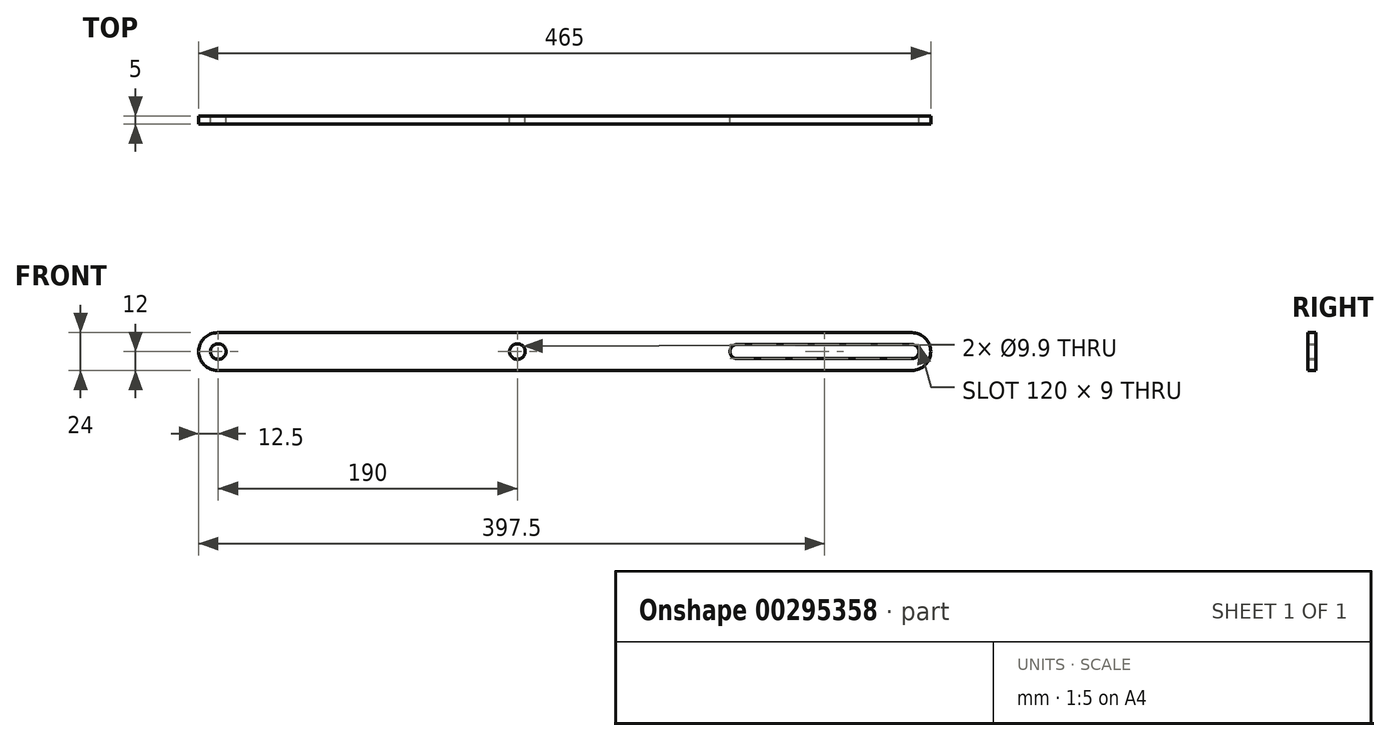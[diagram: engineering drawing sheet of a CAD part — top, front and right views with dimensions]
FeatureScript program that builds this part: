
annotation { "Feature Type Name" : "Feature", "Feature Type Description" : "" }
export const myFeature = defineFeature(function(context is Context, id is Id, definition is map)
    precondition{}
    {
        {
            var Q0;
            Q0=qCreatedBy(makeId("Front.planeOp"),FACE);
            var sketch = newSketch(context, id + "F0", { "sketchPlane" : qUnion([Q0])});
            skLineSegment(sketch, "E0.bottom", {"start": v(220.5, -12) * mm, "end": v(-220.5, -12) * mm});
            skLineSegment(sketch, "E0.top", {"start": v(220.5, 12) * mm, "end": v(-220.5, 12) * mm});
            skLineSegment(sketch, "E0.left", {"start": v(232.5, 0) * mm, "end": v(232.5, 0) * mm});
            skLineSegment(sketch, "E0.right", {"start": v(-232.5, 0) * mm, "end": v(-232.5, 0) * mm});
            skPoint(sketch, "E0.middle", {"position": v(0, 0) * mm});
            skCircle(sketch, "E1", {"center": v(-220, 0) * mm, "radius": 4.95 * mm});
            skLineSegment(sketch, "E2.bottom", {"start": v(220.5, -4.5) * mm, "end": v(109.5, -4.5) * mm});
            skLineSegment(sketch, "E2.top", {"start": v(220.5, 4.5) * mm, "end": v(109.5, 4.5) * mm});
            skLineSegment(sketch, "E2.left", {"start": v(225, 0) * mm, "end": v(225, 0) * mm});
            skLineSegment(sketch, "E2.right", {"start": v(105, 0) * mm, "end": v(105, 0) * mm});
            skPoint(sketch, "E2.middle", {"position": v(165, 0) * mm});
            skCircle(sketch, "E3", {"center": v(-30, 0) * mm, "radius": 4.95 * mm});
            skPoint(sketch, "E4.visualSharp", {"position": v(-232.5, 12) * mm});
            skArc(sketch, "E4.filletArc", {"start": v(-220.5, 12) * mm, "mid": v(-228.99, 8.49) * mm, "end": v(-232.5, 0) * mm});
            skPoint(sketch, "E5.visualSharp", {"position": v(-232.5, -12) * mm});
            skArc(sketch, "E5.filletArc", {"start": v(-232.5, 0) * mm, "mid": v(-228.99, -8.49) * mm, "end": v(-220.5, -12) * mm});
            skPoint(sketch, "E6.visualSharp", {"position": v(232.5, 12) * mm});
            skArc(sketch, "E6.filletArc", {"start": v(232.5, 0) * mm, "mid": v(228.99, 8.49) * mm, "end": v(220.5, 12) * mm});
            skPoint(sketch, "E7.visualSharp", {"position": v(232.5, -12) * mm});
            skArc(sketch, "E7.filletArc", {"start": v(220.5, -12) * mm, "mid": v(228.99, -8.49) * mm, "end": v(232.5, 0) * mm});
            skPoint(sketch, "E8.visualSharp", {"position": v(225, 4.5) * mm});
            skPoint(sketch, "E9.visualSharp", {"position": v(225, -4.5) * mm});
            skPoint(sketch, "E10.visualSharp", {"position": v(105, 4.5) * mm});
            skPoint(sketch, "E11.visualSharp", {"position": v(105, -4.5) * mm});
            skArc(sketch, "E12.filletArc", {"start": v(109.5, 4.5) * mm, "mid": v(106.32, 3.18) * mm, "end": v(105, 0) * mm});
            skArc(sketch, "E13.filletArc", {"start": v(105, 0) * mm, "mid": v(106.32, -3.18) * mm, "end": v(109.5, -4.5) * mm});
            skArc(sketch, "E14.filletArc", {"start": v(225, 0) * mm, "mid": v(223.68, 3.18) * mm, "end": v(220.5, 4.5) * mm});
            skArc(sketch, "E15.filletArc", {"start": v(220.5, -4.5) * mm, "mid": v(223.68, -3.18) * mm, "end": v(225, 0) * mm});
            skSolve(sketch);
        }
        {
            var Q0;
            Q0=makeQuery(id+"F0.imprint","IMPRINT",FACE,{"disambiguationData":[TD([[makeQuery(id+"F0.imprint","IMPRINT",EDGE,{"derivedFrom":sQuery(id+"F0.wireOp",EDGE,"E0.bottom")}),-1.0]])]});
            extrude(context, id + "F1", {"entities" : qUnion([Q0]), "depth" : 5 * mm});
        }
    });
